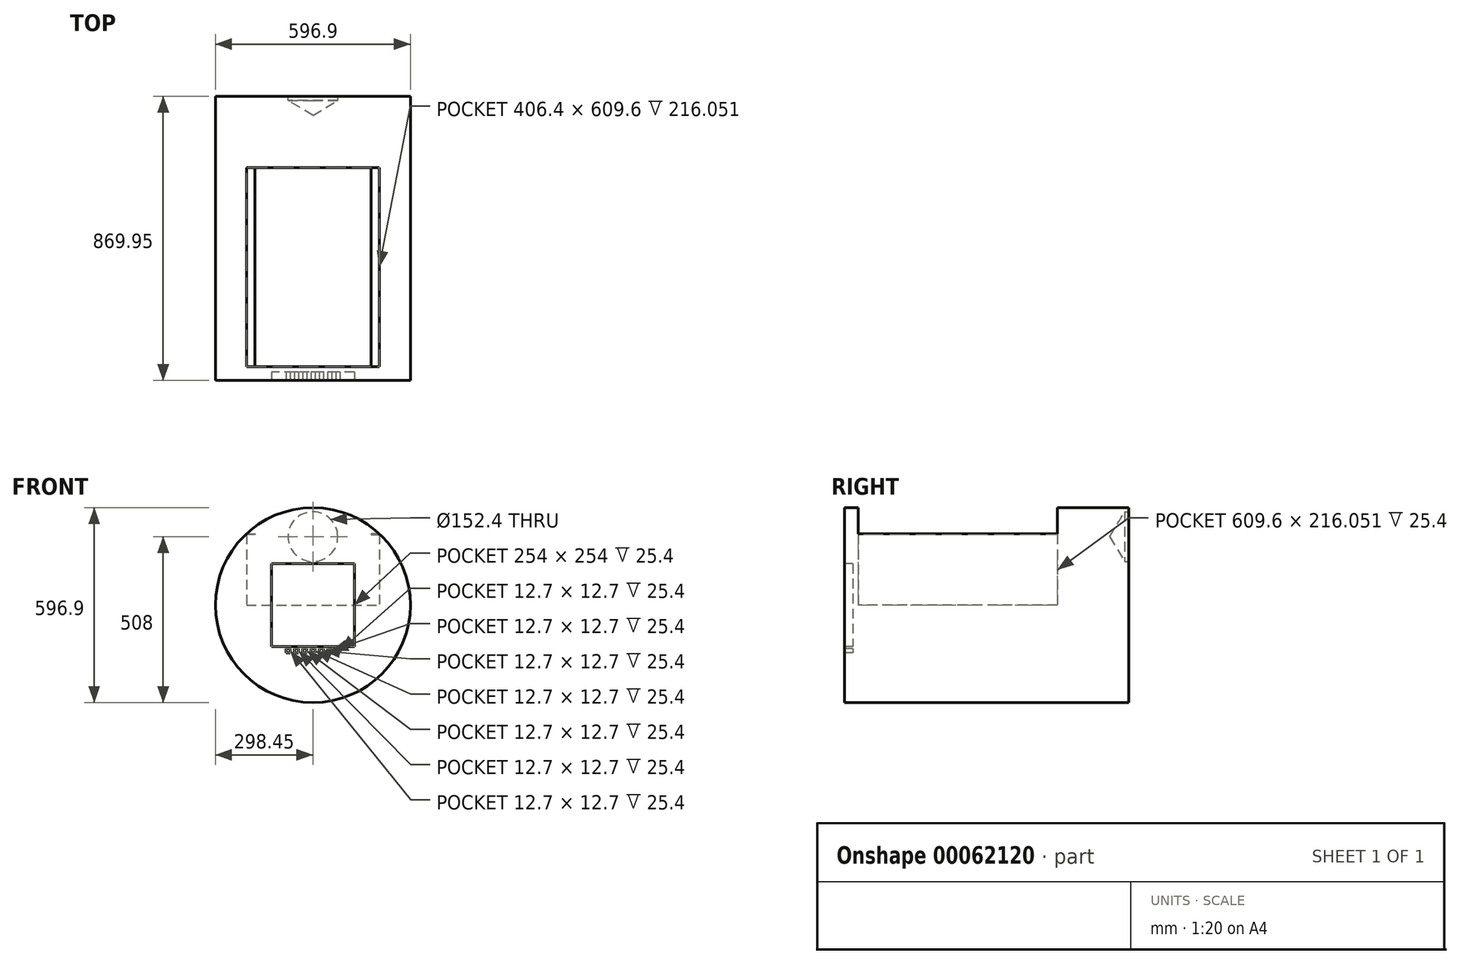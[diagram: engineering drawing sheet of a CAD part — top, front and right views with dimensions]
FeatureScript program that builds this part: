
annotation { "Feature Type Name" : "Feature", "Feature Type Description" : "" }
export const myFeature = defineFeature(function(context is Context, id is Id, definition is map)
    precondition{}
    {
        {
            var Q0;
            Q0=qCreatedBy(makeId("Front.planeOp"),FACE);
            var sketch = newSketch(context, id + "F0", { "sketchPlane" : qUnion([Q0])});
            skCircle(sketch, "E0", {"center": v(0, 0) * mm, "radius": 298.45 * mm});
            skSolve(sketch);
        }
        {
            var Q0;
            Q0=makeQuery(id+"F0.imprint","IMPRINT",FACE,{"disambiguationData":[TD([[makeQuery(id+"F0.imprint","IMPRINT",EDGE,{"derivedFrom":sQuery(id+"F0.wireOp",EDGE,"E0")}),1.0]])]});
            extrude(context, id + "F1", {"entities" : qUnion([Q0]), "oppositeDirection" : true, "depth" : 869.95 * mm});
        }
        {
            var Q0;
            Q0=qCreatedBy(makeId("Top.planeOp"),FACE);
            var sketch = newSketch(context, id + "F2", { "sketchPlane" : qUnion([Q0])});
            skLineSegment(sketch, "E1.bottom", {"start": v(-203.2, 651.38) * mm, "end": v(203.2, 651.38) * mm});
            skLineSegment(sketch, "E1.top", {"start": v(-203.2, 41.78) * mm, "end": v(203.2, 41.78) * mm});
            skLineSegment(sketch, "E1.left", {"start": v(-203.2, 651.38) * mm, "end": v(-203.2, 41.78) * mm});
            skLineSegment(sketch, "E1.right", {"start": v(203.2, 651.38) * mm, "end": v(203.2, 41.78) * mm});
            skSolve(sketch);
        }
        {
            var Q0;
            Q0=makeQuery(id+"F1.opExtrude","CAP_FACE",FACE,{"disambiguationData":[OSD([sQuery(id+"F0.wireOp",EDGE,"E0")])],"isStart":false});
            var sketch = newSketch(context, id + "F3", { "sketchPlane" : qUnion([Q0])});
            skLineSegment(sketch, "E2", {"start": v(0, 0) * mm, "end": v(0, 209.55) * mm});
            skCircle(sketch, "E3", {"center": v(0, 209.55) * mm, "radius": 76.2 * mm});
            skSolve(sketch);
        }
        {
            var Q0;
            Q0=sQuery(id+"F3.wireOp",VERTEX,"E3.center");
            var Q1;
            Q1=makeQuery(id+"F1.opExtrude","SWEPT_BODY",BODY,{"disambiguationData":[OSD([sQuery(id+"F0.wireOp",EDGE,"E0")])]});
            hole(context, id + "F4", {"style" : HoleStyle.SIMPLE, "endStyle" : HoleEndStyle.BLIND, "holeDiameter" : 152.4 * mm, "holeDepth" : 12.7 * mm, "isTappedThrough" : true, "tappedDepth" : 12.7 * mm, "tapClearance" : 3, "locations" : qUnion([Q0]), "scope" : qUnion([Q1])});
        }
        {
            var Q0;
            Q0=makeQuery(id+"F1.opExtrude","CAP_FACE",FACE,{"disambiguationData":[OSD([sQuery(id+"F0.wireOp",EDGE,"E0")])],"isStart":true});
            var sketch = newSketch(context, id + "F5", { "sketchPlane" : qUnion([Q0])});
            skLineSegment(sketch, "E4.bottom", {"start": v(127, 127) * mm, "end": v(-127, 127) * mm});
            skLineSegment(sketch, "E4.top", {"start": v(127, -127) * mm, "end": v(-127, -127) * mm});
            skLineSegment(sketch, "E4.left", {"start": v(127, 127) * mm, "end": v(127, -127) * mm});
            skLineSegment(sketch, "E4.right", {"start": v(-127, 127) * mm, "end": v(-127, -127) * mm});
            skPoint(sketch, "E4.middle", {"position": v(0, 0) * mm});
            skLineSegment(sketch, "E5", {"start": v(0, -127) * mm, "end": v(0, -139.7) * mm});
            skPoint(sketch, "E5.endSnap0", {"position": v(0, -127) * mm});
            skLineSegment(sketch, "E6.bottom", {"start": v(6.35, -133.35) * mm, "end": v(-6.35, -133.35) * mm});
            skLineSegment(sketch, "E6.top", {"start": v(6.35, -146.05) * mm, "end": v(-6.35, -146.05) * mm});
            skLineSegment(sketch, "E6.left", {"start": v(6.35, -133.35) * mm, "end": v(6.35, -146.05) * mm});
            skLineSegment(sketch, "E6.right", {"start": v(-6.35, -133.35) * mm, "end": v(-6.35, -146.05) * mm});
            skPoint(sketch, "E6.middle", {"position": v(0, -139.7) * mm});
            skLineSegment(sketch, "E7.1.0.0", {"start": v(19.05, -133.35) * mm, "end": v(19.05, -146.05) * mm});
            skLineSegment(sketch, "E7.1.0.1", {"start": v(31.75, -133.35) * mm, "end": v(19.05, -133.35) * mm});
            skLineSegment(sketch, "E7.1.0.2", {"start": v(31.75, -146.05) * mm, "end": v(19.05, -146.05) * mm});
            skLineSegment(sketch, "E7.1.0.3", {"start": v(31.75, -133.35) * mm, "end": v(31.75, -146.05) * mm});
            skLineSegment(sketch, "E7.2.0.0", {"start": v(44.45, -133.35) * mm, "end": v(44.45, -146.05) * mm});
            skLineSegment(sketch, "E7.2.0.1", {"start": v(57.15, -133.35) * mm, "end": v(44.45, -133.35) * mm});
            skLineSegment(sketch, "E7.2.0.2", {"start": v(57.15, -146.05) * mm, "end": v(44.45, -146.05) * mm});
            skLineSegment(sketch, "E7.2.0.3", {"start": v(57.15, -133.35) * mm, "end": v(57.15, -146.05) * mm});
            skLineSegment(sketch, "E7.3.0.0", {"start": v(69.85, -133.35) * mm, "end": v(69.85, -146.05) * mm});
            skLineSegment(sketch, "E7.3.0.1", {"start": v(82.55, -133.35) * mm, "end": v(69.85, -133.35) * mm});
            skLineSegment(sketch, "E7.3.0.2", {"start": v(82.55, -146.05) * mm, "end": v(69.85, -146.05) * mm});
            skLineSegment(sketch, "E7.3.0.3", {"start": v(82.55, -133.35) * mm, "end": v(82.55, -146.05) * mm});
            skLineSegment(sketch, "E8.1.0.0", {"start": v(-31.75, -133.35) * mm, "end": v(-31.75, -146.05) * mm});
            skLineSegment(sketch, "E8.1.0.1", {"start": v(-19.05, -133.35) * mm, "end": v(-19.05, -146.05) * mm});
            skLineSegment(sketch, "E8.1.0.2", {"start": v(-19.05, -133.35) * mm, "end": v(-31.75, -133.35) * mm});
            skLineSegment(sketch, "E8.2.0.0", {"start": v(-57.15, -133.35) * mm, "end": v(-57.15, -146.05) * mm});
            skLineSegment(sketch, "E8.2.0.1", {"start": v(-44.45, -133.35) * mm, "end": v(-44.45, -146.05) * mm});
            skLineSegment(sketch, "E8.2.0.2", {"start": v(-44.45, -133.35) * mm, "end": v(-57.15, -133.35) * mm});
            skLineSegment(sketch, "E8.3.0.0", {"start": v(-82.55, -133.35) * mm, "end": v(-82.55, -146.05) * mm});
            skLineSegment(sketch, "E8.3.0.1", {"start": v(-69.85, -133.35) * mm, "end": v(-69.85, -146.05) * mm});
            skLineSegment(sketch, "E8.3.0.2", {"start": v(-69.85, -133.35) * mm, "end": v(-82.55, -133.35) * mm});
            skLineSegment(sketch, "E9", {"start": v(-82.55, -146.05) * mm, "end": v(-69.85, -146.05) * mm});
            skLineSegment(sketch, "E10", {"start": v(-57.15, -146.05) * mm, "end": v(-44.45, -146.05) * mm});
            skLineSegment(sketch, "E11", {"start": v(-31.75, -146.05) * mm, "end": v(-19.05, -146.05) * mm});
            skSolve(sketch);
        }
        {
            var Q0;
            Q0=makeQuery(id+"F5.imprint","IMPRINT",FACE,{"disambiguationData":[TD([[makeQuery(id+"F5.imprint","IMPRINT",EDGE,{"derivedFrom":sQuery(id+"F5.wireOp",EDGE,"E4.bottom")}),1.0]])]});
            extrude(context, id + "F6", {"entities" : qUnion([Q0]), "operationType" : NewBodyOperationType.REMOVE, "oppositeDirection" : true, "depth" : 25.4 * mm});
        }
        {
            var Q0;
            Q0=makeQuery(id+"F5.imprint","IMPRINT",FACE,{"disambiguationData":[TD([[makeQuery(id+"F5.imprint","IMPRINT",EDGE,{"derivedFrom":sQuery(id+"F5.wireOp",EDGE,"E8.3.0.0")}),1.0]])]});
            var Q1;
            Q1=makeQuery(id+"F5.imprint","IMPRINT",FACE,{"disambiguationData":[TD([[makeQuery(id+"F5.imprint","IMPRINT",EDGE,{"derivedFrom":sQuery(id+"F5.wireOp",EDGE,"E8.2.0.0")}),1.0]])]});
            var Q2;
            Q2=makeQuery(id+"F5.imprint","IMPRINT",FACE,{"disambiguationData":[TD([[makeQuery(id+"F5.imprint","IMPRINT",EDGE,{"derivedFrom":sQuery(id+"F5.wireOp",EDGE,"E8.1.0.0")}),1.0]])]});
            var Q3;
            Q3=makeQuery(id+"F5.imprint","IMPRINT",FACE,{"disambiguationData":[TD([[makeQuery(id+"F5.imprint","IMPRINT",EDGE,{"derivedFrom":sQuery(id+"F5.wireOp",EDGE,"E6.top")}),-1.0]])]});
            var Q4;
            Q4=makeQuery(id+"F5.imprint","IMPRINT",FACE,{"disambiguationData":[TD([[makeQuery(id+"F5.imprint","IMPRINT",EDGE,{"derivedFrom":sQuery(id+"F5.wireOp",EDGE,"E7.1.0.0")}),1.0]])]});
            var Q5;
            Q5=makeQuery(id+"F5.imprint","IMPRINT",FACE,{"disambiguationData":[TD([[makeQuery(id+"F5.imprint","IMPRINT",EDGE,{"derivedFrom":sQuery(id+"F5.wireOp",EDGE,"E7.2.0.0")}),1.0]])]});
            var Q6;
            Q6=makeQuery(id+"F5.imprint","IMPRINT",FACE,{"disambiguationData":[TD([[makeQuery(id+"F5.imprint","IMPRINT",EDGE,{"derivedFrom":sQuery(id+"F5.wireOp",EDGE,"E7.3.0.0")}),1.0]])]});
            extrude(context, id + "F7", {"entities" : qUnion([Q0, Q1, Q2, Q3, Q4, Q5, Q6]), "operationType" : NewBodyOperationType.REMOVE, "oppositeDirection" : true, "depth" : 25.4 * mm});
        }
        {
            var Q0;
            Q0 = qSketchRegion(id + "F2", true);
            extrude(context, id + "F8", {"entities" : qUnion([Q0]), "operationType" : NewBodyOperationType.REMOVE, "endBound" : BoundingType.THROUGH_ALL, "depth" : 25.4 * mm, "offsetDistance" : 25.4 * mm});
        }
        {
            var Q0;
            Q0=makeQuery(id+"F8.boolean.opBoolean","COPY",FACE,{"derivedFrom":makeQuery(id+"F8.opExtrude","SWEPT_FACE",FACE,{"disambiguationData":[OSD([sQuery(id+"F2.wireOp",EDGE,"E1.bottom")])]})});
            var sketch = newSketch(context, id + "F9", { "sketchPlane" : qUnion([Q0])});
            skLineSegment(sketch, "E12", {"start": v(-203.2, 218.6) * mm, "end": v(-177.8, 218.6) * mm});
            skLineSegment(sketch, "E13", {"start": v(-177.8, 218.6) * mm, "end": v(-177.8, 216.05) * mm});
            skLineSegment(sketch, "E14", {"start": v(-177.8, 216.05) * mm, "end": v(-205.71, 216.05) * mm});
            skLineSegment(sketch, "E15", {"start": v(-205.71, 216.05) * mm, "end": v(-203.2, 218.6) * mm});
            skLineSegment(sketch, "E16.MirrorCS", {"start": v(177.8, 218.6) * mm, "end": v(177.8, 216.05) * mm});
            skLineSegment(sketch, "E17.MirrorCS", {"start": v(205.71, 216.05) * mm, "end": v(203.2, 218.6) * mm});
            skLineSegment(sketch, "E18.MirrorCS", {"start": v(203.2, 218.6) * mm, "end": v(177.8, 218.6) * mm});
            skLineSegment(sketch, "E19.MirrorCS", {"start": v(177.8, 216.05) * mm, "end": v(205.71, 216.05) * mm});
            skSolve(sketch);
        }
        {
            var Q0;
            Q0 = qSketchRegion(id + "F9", true);
            extrude(context, id + "F10", {"entities" : qUnion([Q0]), "operationType" : NewBodyOperationType.ADD, "depth" : 609.6 * mm, "offsetDistance" : 25.4 * mm});
        }
    });
